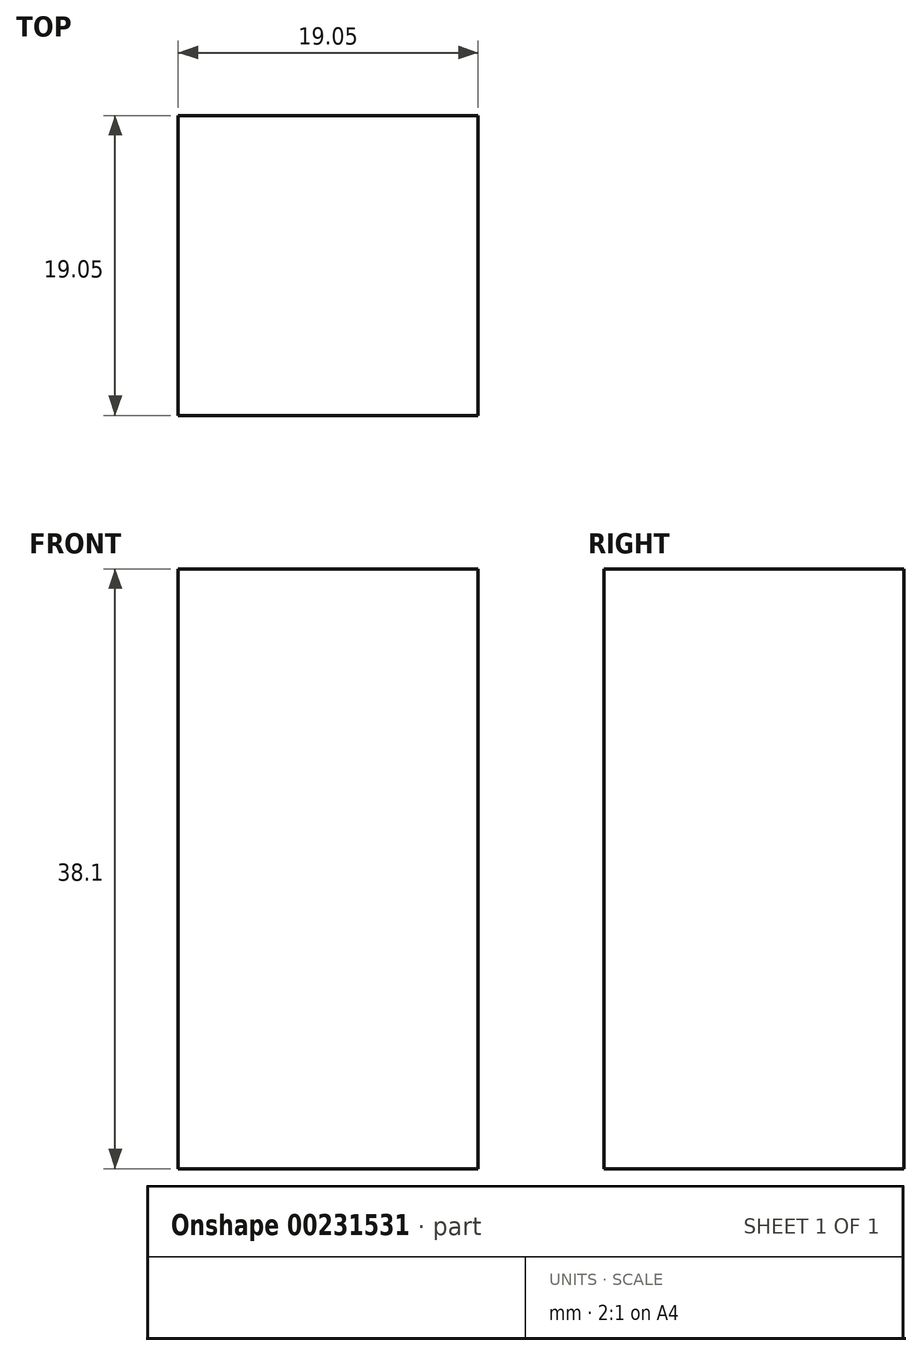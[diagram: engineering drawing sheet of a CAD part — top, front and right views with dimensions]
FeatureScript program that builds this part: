
annotation { "Feature Type Name" : "Feature", "Feature Type Description" : "" }
export const myFeature = defineFeature(function(context is Context, id is Id, definition is map)
    precondition{}
    {
        {
            var Q0;
            Q0=qCreatedBy(makeId("Front.planeOp"),FACE);
            var sketch = newSketch(context, id + "F0", { "sketchPlane" : qUnion([Q0])});
            skLineSegment(sketch, "E0.bottom", {"start": v(-9.32, 21.95) * mm, "end": v(9.73, 21.95) * mm});
            skLineSegment(sketch, "E0.top", {"start": v(-9.32, -16.15) * mm, "end": v(9.73, -16.15) * mm});
            skLineSegment(sketch, "E0.left", {"start": v(-9.32, 21.95) * mm, "end": v(-9.32, -16.15) * mm});
            skLineSegment(sketch, "E0.right", {"start": v(9.73, 21.95) * mm, "end": v(9.73, -16.15) * mm});
            skSolve(sketch);
        }
        {
            var Q0;
            Q0 = qSketchRegion(id + "F0", true);
            extrude(context, id + "F1", {"entities" : qUnion([Q0]), "depth" : 19.05 * mm});
        }
    });
